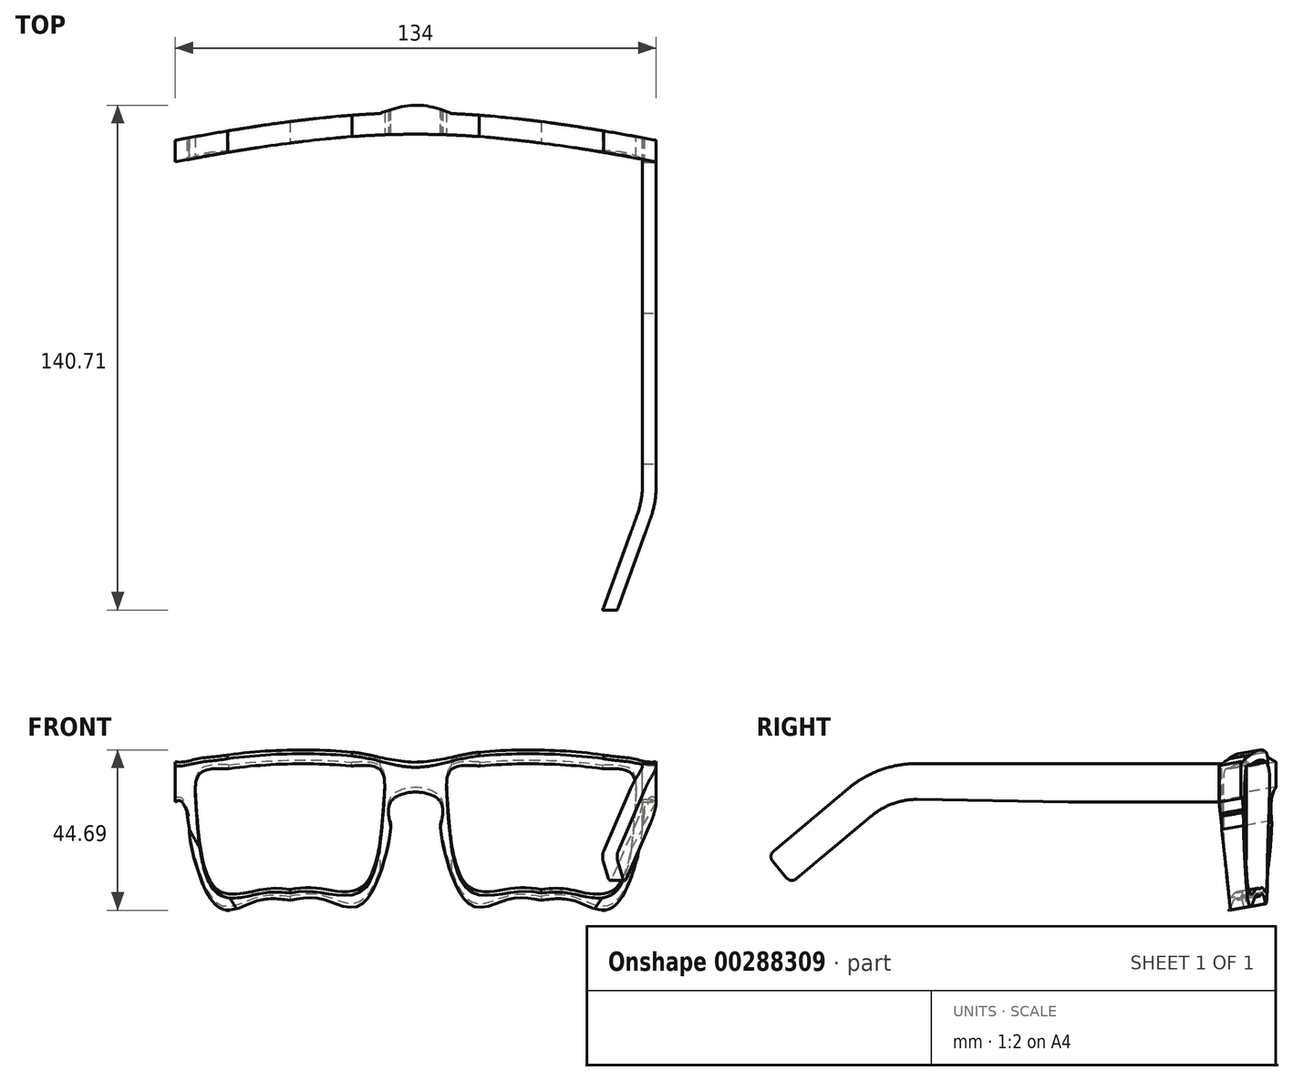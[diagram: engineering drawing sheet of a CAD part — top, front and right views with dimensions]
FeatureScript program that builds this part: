
annotation { "Feature Type Name" : "Feature", "Feature Type Description" : "" }
export const myFeature = defineFeature(function(context is Context, id is Id, definition is map)
    precondition{}
    {
        {
            var Q0;
            Q0=qCreatedBy(makeId("Front.planeOp"),FACE);
            var sketch = newSketch(context, id + "F0", { "sketchPlane" : qUnion([Q0])});
            skLineSegment(sketch, "E0", {"start": v(-67, 0) * mm, "end": v(67, 0) * mm, "construction": true});
            skLineSegment(sketch, "E1", {"start": v(0, -20.5) * mm, "end": v(0, 20.5) * mm, "construction": true});
            skLineSegment(sketch, "E2.bottom", {"start": v(-67, 20.5) * mm, "end": v(67, 20.5) * mm, "construction": true});
            skLineSegment(sketch, "E2.top", {"start": v(-67, -20.5) * mm, "end": v(67, -20.5) * mm, "construction": true});
            skLineSegment(sketch, "E2.left", {"start": v(-67, 20.5) * mm, "end": v(-67, -20.5) * mm, "construction": true});
            skLineSegment(sketch, "E2.right", {"start": v(67, 20.5) * mm, "end": v(67, -20.5) * mm, "construction": true});
            skLineSegment(sketch, "E3", {"start": v(-10, 20.5) * mm, "end": v(10, 20.5) * mm, "construction": true});
            skLineSegment(sketch, "E4", {"start": v(-10, 20.5) * mm, "end": v(-10, -20.5) * mm, "construction": true});
            skLineSegment(sketch, "E5", {"start": v(10, 20.5) * mm, "end": v(10, -20.5) * mm, "construction": true});
            skLineSegment(sketch, "E6", {"start": v(-10, 20.5) * mm, "end": v(-60, 20.5) * mm, "construction": true});
            skLineSegment(sketch, "E7", {"start": v(0, 0) * mm, "end": v(0, 7.8) * mm, "construction": true});
            skLineSegment(sketch, "E8", {"start": v(0, 7.8) * mm, "end": v(0, 15.6) * mm, "construction": true});
            skLineSegment(sketch, "E9", {"start": v(-60, 20.5) * mm, "end": v(-60, -20.5) * mm, "construction": true});
            skLineSegment(sketch, "E10", {"start": v(0, 7.8) * mm, "end": v(-67, 7.8) * mm, "construction": true});
            skLineSegment(sketch, "E11.MirrorCS", {"start": v(0, 15.6) * mm, "end": v(67, 15.6) * mm, "construction": true});
            skLineSegment(sketch, "E12.MirrorCS", {"start": v(0, 7.8) * mm, "end": v(67, 7.8) * mm, "construction": true});
            skPoint(sketch, "E13", {"position": v(-71.63, 0) * mm});
            skPoint(sketch, "E14", {"position": v(-10, 0) * mm});
            skLineSegment(sketch, "E15", {"start": v(-60, 0) * mm, "end": v(-10, 0) * mm, "construction": true});
            skPoint(sketch, "E16", {"position": v(-35, 0) * mm});
            skLineSegment(sketch, "E17", {"start": v(-35, 20.5) * mm, "end": v(-35, -20.5) * mm, "construction": true});
            skLineSegment(sketch, "E18", {"start": v(-35, -20.5) * mm, "end": v(-35, -18.5) * mm, "construction": true});
            skLineSegment(sketch, "E19", {"start": v(-35, -18.5) * mm, "end": v(-35, 17.5) * mm, "construction": true});
            skLineSegment(sketch, "E20", {"start": v(-60, 17.5) * mm, "end": v(-10, 17.5) * mm, "construction": true});
            skLineSegment(sketch, "E21", {"start": v(-35, -18.5) * mm, "end": v(-67, -18.5) * mm, "construction": true});
            skArc(sketch, "E22", {"start": v(-17.95, 16.62) * mm, "mid": v(-35, 17.5) * mm, "end": v(-52.05, 16.62) * mm});
            skFitSpline(sketch, "E23", {"points": [v(-52.05, 16.62) * mm, v(-60, 5.42) * mm, v(-52.82, -14.3) * mm, v(-35, -18.5) * mm], "startDerivative": vector(-80.93, -10.37) * mm, "endDerivative": vector(67.15, -1.23) * mm});
            skFitSpline(sketch, "E24.MirrorCS", {"points": [v(-17.95, 16.62) * mm, v(-10, 5.42) * mm, v(-17.18, -14.3) * mm, v(-35, -18.5) * mm], "startDerivative": vector(80.93, -10.37) * mm, "endDerivative": vector(-67.15, -1.23) * mm});
            skArc(sketch, "E25.MirrorCS", {"start": v(17.95, 16.62) * mm, "mid": v(35, 17.5) * mm, "end": v(52.05, 16.62) * mm});
            skFitSpline(sketch, "E26.MirrorCS", {"points": [v(17.95, 16.62) * mm, v(10, 5.42) * mm, v(17.18, -14.3) * mm, v(35, -18.5) * mm], "startDerivative": vector(-80.93, -10.37) * mm, "endDerivative": vector(67.15, -1.23) * mm});
            skFitSpline(sketch, "E27.MirrorCS", {"points": [v(52.05, 16.62) * mm, v(60, 5.42) * mm, v(52.82, -14.3) * mm, v(35, -18.5) * mm], "startDerivative": vector(80.93, -10.37) * mm, "endDerivative": vector(-67.15, -1.23) * mm});
            skLineSegment(sketch, "E28", {"start": v(-10, 20.5) * mm, "end": v(-7, 20.5) * mm, "construction": true});
            skLineSegment(sketch, "E29", {"start": v(-7, 20.5) * mm, "end": v(-7, -20.5) * mm, "construction": true});
            skLineSegment(sketch, "E30.MirrorCS", {"start": v(7, 20.5) * mm, "end": v(7, -20.5) * mm, "construction": true});
            skFitSpline(sketch, "E31", {"points": [v(-7, 0) * mm, v(0, 7.8) * mm, v(7, 0) * mm], "startDerivative": vector(0, 38.28) * mm, "endDerivative": vector(0, -38.28) * mm});
            skFitSpline(sketch, "E32", {"points": [v(-7, 0) * mm, v(-15.43, -16.34) * mm, v(-35, -20.5) * mm], "startDerivative": vector(0, -10.94) * mm, "endDerivative": vector(-54.71, 0) * mm});
            skFitSpline(sketch, "E33.MirrorCS", {"points": [v(7, 0) * mm, v(15.43, -16.34) * mm, v(35, -20.5) * mm], "startDerivative": vector(0, -10.94) * mm, "endDerivative": vector(54.71, 0) * mm});
            skFitSpline(sketch, "E34.MirrorCS", {"points": [v(-63, 0) * mm, v(-54.57, -16.34) * mm, v(-35, -20.5) * mm], "startDerivative": vector(0, -10.94) * mm, "endDerivative": vector(54.71, 0) * mm});
            skFitSpline(sketch, "E35", {"points": [v(-67, 7.8) * mm, v(-63.86, 5.01) * mm, v(-63, 0) * mm], "startDerivative": vector(11.64, 0) * mm, "endDerivative": vector(3.34, -25.7) * mm});
            skFitSpline(sketch, "E36.MirrorCS", {"points": [v(67, 7.8) * mm, v(63.86, 5.01) * mm, v(63, 0) * mm], "startDerivative": vector(-11.64, 0) * mm, "endDerivative": vector(-3.34, -25.7) * mm});
            skFitSpline(sketch, "E37.MirrorCS", {"points": [v(63, 0) * mm, v(54.57, -16.34) * mm, v(35, -20.5) * mm], "startDerivative": vector(0, -10.94) * mm, "endDerivative": vector(-54.71, 0) * mm});
            skLineSegment(sketch, "E38", {"start": v(-67, 7.8) * mm, "end": v(-67, 20.5) * mm});
            skArc(sketch, "E39.0", {"start": v(-17.67, 19.4) * mm, "mid": v(-35, 20.3) * mm, "end": v(-52.33, 19.4) * mm});
            skArc(sketch, "E40.MirrorCS", {"start": v(17.67, 19.4) * mm, "mid": v(35, 20.3) * mm, "end": v(52.33, 19.4) * mm});
            skFitSpline(sketch, "E41", {"points": [v(-17.67, 19.4) * mm, v(0, 17.22) * mm, v(17.67, 19.4) * mm], "startDerivative": vector(35.33, -6.54) * mm, "endDerivative": vector(35.33, 6.54) * mm});
            skLineSegment(sketch, "E42", {"start": v(67, 7.8) * mm, "end": v(67, 20.5) * mm});
            skFitSpline(sketch, "E43", {"points": [v(67, 17.98) * mm, v(60.54, 18.48) * mm, v(52.33, 19.4) * mm], "startDerivative": vector(-14.43, -1.07) * mm, "endDerivative": vector(-15.93, 1.9) * mm});
            skFitSpline(sketch, "E44.MirrorCS", {"points": [v(-67, 17.98) * mm, v(-60.54, 18.48) * mm, v(-52.33, 19.4) * mm], "startDerivative": vector(14.43, -1.07) * mm, "endDerivative": vector(15.93, 1.9) * mm});
            skSolve(sketch);
        }
        {
            var Q0;
            Q0=qCreatedBy(makeId("Right.planeOp"),FACE);
            var sketch = newSketch(context, id + "F1", { "sketchPlane" : qUnion([Q0])});
            skFitSpline(sketch, "E45.0", {"points": [v(0, 16.62) * mm, v(0, 15.6) * mm, v(0, 5.41) * mm, v(0, -18.1) * mm, v(0, -18.36) * mm, v(0, -18.5) * mm]});
            skPoint(sketch, "E46.0", {"position": v(0, 18.66) * mm});
            skPoint(sketch, "E47.0", {"position": v(0, 20.5) * mm});
            skPoint(sketch, "E48.0", {"position": v(0, -20.5) * mm});
            skLineSegment(sketch, "E49", {"start": v(0, 20.5) * mm, "end": v(46.17, 20.5) * mm, "construction": true});
            skLineSegment(sketch, "E50", {"start": v(0, 20.5) * mm, "end": v(7.4, -21.44) * mm, "construction": true});
            skSolve(sketch);
        }
        {
            var Q0;
            Q0=sQuery(id+"F1.wireOp",EDGE,"E50");
            var Q1;
            Q1=qCreatedBy(makeId("Front.planeOp"),FACE);
            cPlane(context, id + "F2", {"entities" : qUnion([Q0, Q1]), "cplaneType" : CPlaneType.LINE_ANGLE, "offset" : 25.4 * mm, "angle" : 0 * degree, "width" : 152.4 * mm, "height" : 152.4 * mm});
        }
        {
            var Q0;
            Q0=qCreatedBy(id+"F2.planeOp",FACE);
            var sketch = newSketch(context, id + "F3", { "sketchPlane" : qUnion([Q0])});
            skPoint(sketch, "E51.0", {"position": v(-67, 7.68) * mm});
            skPoint(sketch, "E52.0", {"position": v(-63.72, 4.64) * mm});
            skFitSpline(sketch, "E53.0", {"points": [v(-67, 7.68) * mm, v(-65.15, 7.68) * mm, v(-63.28, 3.66) * mm, v(-63.58, 4.42) * mm, v(-63, 0) * mm]});
            skFitSpline(sketch, "E54.0", {"points": [v(-63, 0) * mm, v(-63, -1.76) * mm, v(-55.1, -21.6) * mm, v(-44.31, -20.19) * mm, v(-35, -20.19) * mm]});
            skFitSpline(sketch, "E55.0", {"points": [v(-7, 0) * mm, v(-7, -1.76) * mm, v(-14.9, -21.6) * mm, v(-25.69, -20.19) * mm, v(-35, -20.19) * mm]});
            skFitSpline(sketch, "E56.0", {"points": [v(7, 0) * mm, v(7, 6.28) * mm, v(0, 9.08) * mm, v(-7, 6.28) * mm, v(-7, 0) * mm]});
            skFitSpline(sketch, "E57.0", {"points": [v(7, 0) * mm, v(7, -1.76) * mm, v(14.9, -21.6) * mm, v(25.69, -20.19) * mm, v(35, -20.19) * mm]});
            skFitSpline(sketch, "E58.0", {"points": [v(63, 0) * mm, v(63, -1.76) * mm, v(55.1, -21.6) * mm, v(44.31, -20.19) * mm, v(35, -20.19) * mm]});
            skFitSpline(sketch, "E59.0", {"points": [v(67, 7.68) * mm, v(65.15, 7.68) * mm, v(63.28, 3.66) * mm, v(63.58, 4.42) * mm, v(63, 0) * mm]});
            skEllipticalArc(sketch, "E60.0", {});
            skFitSpline(sketch, "E61.0", {"points": [v(17.67, 19.1) * mm, v(11.78, 18.03) * mm, v(0, 15.88) * mm, v(-11.78, 18.03) * mm, v(-17.67, 19.1) * mm]});
            skEllipticalArc(sketch, "E62.0", {});
            skFitSpline(sketch, "E63.0", {"points": [v(-52.05, 16.37) * mm, v(-60, 15.36) * mm, v(-61.12, 5.33) * mm, v(-55.22, -17.83) * mm, v(-42.62, -18.08) * mm, v(-35, -18.22) * mm]});
            skFitSpline(sketch, "E64.0", {"points": [v(-17.95, 16.37) * mm, v(-10, 15.36) * mm, v(-8.88, 5.33) * mm, v(-14.78, -17.83) * mm, v(-27.38, -18.08) * mm, v(-35, -18.22) * mm]});
            skFitSpline(sketch, "E65.0", {"points": [v(-17.95, 16.37) * mm, v(-10, 15.36) * mm, v(-8.88, 5.33) * mm, v(-14.78, -17.83) * mm, v(-27.38, -18.08) * mm, v(-35, -18.22) * mm]});
            skFitSpline(sketch, "E66.0", {"points": [v(17.95, 16.37) * mm, v(10, 15.36) * mm, v(8.88, 5.33) * mm, v(14.78, -17.83) * mm, v(27.38, -18.08) * mm, v(35, -18.22) * mm]});
            skFitSpline(sketch, "E67.0", {"points": [v(52.05, 16.37) * mm, v(60, 15.36) * mm, v(61.12, 5.33) * mm, v(55.22, -17.83) * mm, v(42.62, -18.08) * mm, v(35, -18.22) * mm]});
            skFitSpline(sketch, "E68.0", {"points": [v(-67, 17.7) * mm, v(-64.74, 17.54) * mm, v(-60.55, 18.32) * mm, v(-55.15, 18.77) * mm, v(-52.33, 19.1) * mm]});
            skFitSpline(sketch, "E69.0", {"points": [v(67, 17.7) * mm, v(64.74, 17.54) * mm, v(60.55, 18.32) * mm, v(55.15, 18.77) * mm, v(52.33, 19.1) * mm]});
            skEllipticalArc(sketch, "E70.0.0", {});
            skFitSpline(sketch, "E70.0.1", {"points": [v(-17.67, 19.1) * mm, v(-11.78, 18.03) * mm, v(0, 15.88) * mm, v(11.78, 18.03) * mm, v(17.67, 19.1) * mm]});
            skFitSpline(sketch, "E70.0.3", {"points": [v(52.33, 19.1) * mm, v(55.15, 18.77) * mm, v(60.55, 18.32) * mm, v(64.74, 17.54) * mm, v(67, 17.7) * mm]});
            skLineSegment(sketch, "E70.0.4", {"start": v(67, 17.7) * mm, "end": v(67, 7.68) * mm});
            skFitSpline(sketch, "E70.0.5", {"points": [v(67, 7.68) * mm, v(65.15, 7.68) * mm, v(63.28, 3.66) * mm, v(63.58, 4.42) * mm, v(63, 0) * mm]});
            skFitSpline(sketch, "E70.0.6", {"points": [v(63, 0) * mm, v(63, -1.76) * mm, v(55.1, -21.6) * mm, v(44.31, -20.19) * mm, v(35, -20.19) * mm]});
            skFitSpline(sketch, "E70.0.7", {"points": [v(35, -20.19) * mm, v(25.69, -20.19) * mm, v(14.9, -21.6) * mm, v(7, -1.76) * mm, v(7, 0) * mm]});
            skFitSpline(sketch, "E70.0.8", {"points": [v(7, 0) * mm, v(7, 6.28) * mm, v(0, 9.08) * mm, v(-7, 6.28) * mm, v(-7, 0) * mm]});
            skFitSpline(sketch, "E70.0.9", {"points": [v(-7, 0) * mm, v(-7, -1.76) * mm, v(-14.9, -21.6) * mm, v(-25.69, -20.19) * mm, v(-35, -20.19) * mm]});
            skFitSpline(sketch, "E70.0.10", {"points": [v(-35, -20.19) * mm, v(-44.31, -20.19) * mm, v(-55.1, -21.6) * mm, v(-63, -1.76) * mm, v(-63, 0) * mm]});
            skFitSpline(sketch, "E70.0.11", {"points": [v(-63, 0) * mm, v(-63.58, 4.42) * mm, v(-63.28, 3.66) * mm, v(-65.15, 7.68) * mm, v(-67, 7.68) * mm]});
            skLineSegment(sketch, "E70.0.12", {"start": v(-67, 7.68) * mm, "end": v(-67, 17.7) * mm});
            skFitSpline(sketch, "E70.0.13", {"points": [v(-67, 17.7) * mm, v(-64.74, 17.54) * mm, v(-60.55, 18.32) * mm, v(-55.15, 18.77) * mm, v(-52.33, 19.1) * mm]});
            const initialGuessF3  = {"E60.0": [0.035, -0.14567639106445007, 1, 0, 0.1682176836736388, 0.1656620790755546, 1.467573942796451, 1.6740187107933424], "E62.0": [-0.035, -0.14567639106445007, -1, 0, 0.1682176836736388, 0.1656620790755546, 4.609166596386244, 4.815611364383136], "E62.0": [-0.035, -0.14567639106445007, -1, 0, 0.16542368421031978, 0.1629105267421661, 4.6091665963862285, 4.81561136438315], "E60.0": [0.035, -0.14567639106445007, 1, 0, 0.16542368421031978, 0.1629105267421661, 1.4675739427964356, 1.6740187107933577], "E70.0.0": [-0.035, -0.14567639106445007, 1, 0, 0.1682176836736388, 0.1656620790755546, 1.467573942796343, 1.6740187107934503], "E60.0": [0.035, -0.14567639106445007, 1, 0, 0.1682176836736388, 0.1656620790755546, 1.467573942796343, 1.6740187107934503]};
            skSetInitialGuess(sketch, initialGuessF3);
            skSolve(sketch);
        }
        {
            var Q0;
            Q0 = qSketchRegion(id + "F3", true);
            extrude(context, id + "F4", {"entities" : qUnion([Q0]), "depth" : 19.8 * mm, "hasSecondDirection" : true, "secondDirectionOppositeDirection" : true, "secondDirectionDepth" : 15.5 * mm});
        }
        {
            var Q0;
            Q0=qCreatedBy(makeId("Top.planeOp"),FACE);
            var sketch = newSketch(context, id + "F5", { "sketchPlane" : qUnion([Q0])});
            skPoint(sketch, "E71.0.internal.snap0", {"position": v(-82.32, 2.82) * mm});
            skPoint(sketch, "E71.2.internal.snap0", {"position": v(82.43, 2.82) * mm});
            skFitSpline(sketch, "E71", {"points": [v(-82.32, 0) * mm, v(0, 10.6) * mm, v(82.43, 0) * mm], "startDerivative": vector(164.67, 31.78) * mm, "endDerivative": vector(164.84, -31.78) * mm});
            skFitSpline(sketch, "E72.0", {"points": [v(-81.18, -5.9) * mm, v(-74.32, -4.57) * mm, v(-60.65, -1.93) * mm, v(-43.67, 0.94) * mm, v(-30.15, 2.73) * mm, v(-20.05, 3.77) * mm, v(-11.67, 4.32) * mm, v(-4.98, 4.55) * mm, v(0.03, 4.61) * mm, v(5.03, 4.55) * mm, v(11.73, 4.32) * mm, v(20.11, 3.76) * mm, v(30.22, 2.73) * mm, v(43.74, 0.94) * mm, v(60.74, -1.93) * mm, v(74.43, -4.57) * mm, v(81.3, -5.9) * mm]});
            skFitSpline(sketch, "E73", {"points": [v(-10, 10.37) * mm, v(0, 12.7) * mm, v(10, 10.37) * mm], "startDerivative": vector(30, 11.53) * mm, "endDerivative": vector(30, -12.13) * mm});
            skFitSpline(sketch, "E74", {"points": [v(-5, 4.53) * mm, v(0, 5.51) * mm, v(5, 4.53) * mm], "startDerivative": vector(10, 2.93) * mm, "endDerivative": vector(10, -2.93) * mm});
            skFitSpline(sketch, "E75.trimOffspring", {"points": [v(-81.18, -5.9) * mm, v(-74.32, -4.57) * mm, v(-60.65, -1.93) * mm, v(-43.67, 0.94) * mm, v(-30.15, 2.73) * mm, v(-20.05, 3.77) * mm, v(-11.67, 4.32) * mm, v(-4.98, 4.55) * mm, v(0.03, 4.61) * mm, v(5.03, 4.55) * mm, v(11.73, 4.32) * mm, v(20.11, 3.76) * mm, v(30.22, 2.73) * mm, v(43.74, 0.94) * mm, v(60.74, -1.93) * mm, v(74.43, -4.57) * mm, v(81.3, -5.9) * mm]});
            skLineSegment(sketch, "E76", {"start": v(-82.32, 0) * mm, "end": v(-81.18, -5.9) * mm});
            skLineSegment(sketch, "E77", {"start": v(81.3, -5.9) * mm, "end": v(82.43, 0) * mm});
            skSolve(sketch);
        }
        {
            var Q0;
            Q0 = qSketchRegion(id + "F5", true);
            extrude(context, id + "F6", {"entities" : qUnion([Q0]), "operationType" : NewBodyOperationType.INTERSECT, "depth" : 47.75 * mm, "hasSecondDirection" : true, "secondDirectionOppositeDirection" : true, "secondDirectionDepth" : 62.74 * mm});
        }
        {
            var Q0;
            Q0=qCreatedBy(makeId("Top.planeOp"),FACE);
            var Q1;
            Q1=sQuery(id+"F0.wireOp",VERTEX,"E44.MirrorCS.0.internal");
            cPlane(context, id + "F7", {"entities" : qUnion([Q0, Q1]), "cplaneType" : CPlaneType.PLANE_POINT, "offset" : 25.4 * mm, "width" : 152.4 * mm, "height" : 152.4 * mm});
        }
        {
            var Q0;
            Q0=qCreatedBy(id+"F7.planeOp",FACE);
            var sketch = newSketch(context, id + "F8", { "sketchPlane" : qUnion([Q0])});
            skLineSegment(sketch, "E78.0.0", {"start": v(-52.33, -0.55) * mm, "end": v(-52.33, 5.53) * mm});
            skLineSegment(sketch, "E79.0.1", {"start": v(-52.33, 5.53) * mm, "end": v(-52.33, -0.55) * mm});
            skLineSegment(sketch, "E79.0.3", {"start": v(-17.67, 3.9) * mm, "end": v(-17.67, 9.91) * mm});
            skLineSegment(sketch, "E80.0.0", {"start": v(17.67, 3.9) * mm, "end": v(17.67, 9.92) * mm});
            skLineSegment(sketch, "E80.0.4", {"start": v(-17.67, 9.91) * mm, "end": v(-17.67, 3.9) * mm});
            skLineSegment(sketch, "E81.0.0", {"start": v(17.67, 9.92) * mm, "end": v(17.67, 3.9) * mm});
            skLineSegment(sketch, "E81.0.2", {"start": v(52.33, -0.54) * mm, "end": v(52.33, 5.54) * mm});
            skLineSegment(sketch, "E82.0.3", {"start": v(52.33, 5.54) * mm, "end": v(52.33, -0.54) * mm});
            skLineSegment(sketch, "E83", {"start": v(-67, -3.18) * mm, "end": v(-67, -98.18) * mm});
            skLineSegment(sketch, "E84", {"start": v(-67, -138.18) * mm, "end": v(-63.2, -138.18) * mm});
            skLineSegment(sketch, "E85", {"start": v(-63.2, -93) * mm, "end": v(-63.2, -2.48) * mm});
            skLineSegment(sketch, "E86", {"start": v(-65.47, -102.39) * mm, "end": v(-52.44, -138.18) * mm});
            skLineSegment(sketch, "E87.0", {"start": v(-61.67, -101.7) * mm, "end": v(-48.86, -136.88) * mm});
            skLineSegment(sketch, "E88", {"start": v(-52.44, -138.18) * mm, "end": v(-48.86, -136.88) * mm});
            skPoint(sketch, "E89.visualSharp", {"position": v(-63.2, -97.48) * mm});
            skArc(sketch, "E89.filletArc", {"start": v(-63.2, -93) * mm, "mid": v(-62.81, -97.41) * mm, "end": v(-61.67, -101.7) * mm});
            skPoint(sketch, "E90.visualSharp", {"position": v(-67, -98.18) * mm});
            skArc(sketch, "E90.filletArc", {"start": v(-67, -93.7) * mm, "mid": v(-66.61, -98.11) * mm, "end": v(-65.47, -102.39) * mm});
            skFitSpline(sketch, "E91.0", {"points": [v(-52.33, -0.55) * mm, v(-53.55, -0.76) * mm, v(-56, -1.18) * mm, v(-59.67, -1.83) * mm, v(-63.3, -2.5) * mm, v(-65.76, -2.95) * mm, v(-67, -3.18) * mm]});
            skLineSegment(sketch, "E92.MirrorCS", {"start": v(67, -3.18) * mm, "end": v(67, -98.18) * mm});
            skLineSegment(sketch, "E93.MirrorCS", {"start": v(63.2, -93) * mm, "end": v(63.2, -2.48) * mm});
            skArc(sketch, "E94.MirrorCS", {"start": v(67, -93.7) * mm, "mid": v(66.61, -98.11) * mm, "end": v(65.47, -102.39) * mm});
            skArc(sketch, "E95.MirrorCS", {"start": v(63.2, -93) * mm, "mid": v(62.81, -97.41) * mm, "end": v(61.67, -101.7) * mm});
            skLineSegment(sketch, "E96.MirrorCS", {"start": v(65.47, -102.39) * mm, "end": v(52.44, -138.18) * mm});
            skLineSegment(sketch, "E97.MirrorCS", {"start": v(61.67, -101.7) * mm, "end": v(48.86, -136.88) * mm});
            skLineSegment(sketch, "E98.MirrorCS", {"start": v(52.44, -138.18) * mm, "end": v(48.86, -136.88) * mm});
            skLineSegment(sketch, "E99", {"start": v(63.2, -2.48) * mm, "end": v(67, -3.18) * mm});
            skSolve(sketch);
        }
        {
            var Q0;
            {var subQ4=sQuery(id+"F8.wireOp",EDGE,"E85");Q0=makeQuery(id+"F8.imprint","IMPRINT",FACE,{"disambiguationData":[TD([[makeQuery(id+"F8.imprint","IMPRINT",EDGE,{"derivedFrom":subQ4}),1.0]])]});}
            var Q1;
            Q1=makeQuery(id+"F8.imprint","IMPRINT",FACE,{"disambiguationData":[TD([[makeQuery(id+"F8.imprint","IMPRINT",EDGE,{"derivedFrom":sQuery(id+"F8.wireOp",EDGE,"E93.MirrorCS")}),-1.0]])]});
            extrude(context, id + "F9", {"entities" : qUnion([Q0, Q1]), "oppositeDirection" : true, "depth" : 36.58 * mm});
        }
        {
            var Q0;
            Q0=qCreatedBy(makeId("Right.planeOp"),FACE);
            var sketch = newSketch(context, id + "F10", { "sketchPlane" : qUnion([Q0])});
            skLineSegment(sketch, "E100.0.6", {"start": v(-87.26, 17.98) * mm, "end": v(-3.18, 17.98) * mm});
            skLineSegment(sketch, "E101.0.0", {"start": v(-146.92, 17.98) * mm, "end": v(-138.18, 17.98) * mm});
            skLineSegment(sketch, "E101.0.3", {"start": v(-138.18, -18.6) * mm, "end": v(-138.18, 17.98) * mm});
            skLineSegment(sketch, "E102", {"start": v(-3.18, 17.98) * mm, "end": v(-87.26, 17.98) * mm});
            skLineSegment(sketch, "E103", {"start": v(-106.55, 10.96) * mm, "end": v(-127.32, -6.47) * mm, "construction": true});
            skPoint(sketch, "E104.visualSharp", {"position": v(-98.18, 17.98) * mm});
            skArc(sketch, "E104.filletArc", {"start": v(-87.26, 17.98) * mm, "mid": v(-97.52, 16.17) * mm, "end": v(-106.55, 10.96) * mm});
            skLineSegment(sketch, "E105", {"start": v(-106.55, 10.96) * mm, "end": v(-128.82, -7.73) * mm});
            skArc(sketch, "E106.0", {"start": v(-87.26, 7.98) * mm, "mid": v(-94.1, 6.77) * mm, "end": v(-100.12, 3.3) * mm});
            skLineSegment(sketch, "E107", {"start": v(-3.18, 7.24) * mm, "end": v(-45.22, 7.24) * mm, "construction": true});
            skPoint(sketch, "E107.endSnap0", {"position": v(-45.22, 5.98) * mm});
            skLineSegment(sketch, "E108", {"start": v(-45.22, 7.24) * mm, "end": v(-87.26, 7.98) * mm, "construction": true});
            skLineSegment(sketch, "E109.0", {"start": v(-100.12, 3.3) * mm, "end": v(-120.9, -14.13) * mm, "construction": true});
            skLineSegment(sketch, "E110", {"start": v(-3.18, 7.24) * mm, "end": v(-45.22, 7.24) * mm});
            skLineSegment(sketch, "E111", {"start": v(-87.26, 7.98) * mm, "end": v(-45.22, 7.24) * mm});
            skLineSegment(sketch, "E112", {"start": v(-122.4, -15.4) * mm, "end": v(-100.12, 3.3) * mm});
            skLineSegment(sketch, "E113", {"start": v(-123.65, -13.9) * mm, "end": v(-127.56, -9.23) * mm});
            skPoint(sketch, "E114.visualSharp", {"position": v(-122.4, -15.4) * mm});
            skArc(sketch, "E114.filletArc", {"start": v(-123.65, -13.9) * mm, "mid": v(-122.32, -14.59) * mm, "end": v(-120.9, -14.13) * mm});
            skPoint(sketch, "E115.visualSharp", {"position": v(-128.82, -7.73) * mm});
            skArc(sketch, "E115.filletArc", {"start": v(-127.32, -6.47) * mm, "mid": v(-128.01, -7.8) * mm, "end": v(-127.56, -9.23) * mm});
            skLineSegment(sketch, "E116", {"start": v(0, -22.9) * mm, "end": v(-146.92, -22.9) * mm});
            skLineSegment(sketch, "E117", {"start": v(-146.92, -22.9) * mm, "end": v(-146.92, 23.55) * mm});
            skLineSegment(sketch, "E118", {"start": v(-146.92, 23.55) * mm, "end": v(-3.18, 23.55) * mm});
            skLineSegment(sketch, "E119", {"start": v(-3.18, 23.55) * mm, "end": v(-3.18, 17.98) * mm});
            skPoint(sketch, "E120.orphan", {"position": v(-93.7, 17.98) * mm});
            skPoint(sketch, "E121.orphan", {"position": v(-102.39, 17.98) * mm});
            skPoint(sketch, "E100.0.0.end.orphan", {"position": v(2.92, 18.5) * mm});
            skPoint(sketch, "E100.0.2.start.orphan", {"position": v(2.92, 8.32) * mm});
            skPoint(sketch, "E100.0.7.end.orphan", {"position": v(-3.18, 17.42) * mm});
            skLineSegment(sketch, "E122", {"start": v(0, -22.9) * mm, "end": v(-3.18, 7.24) * mm});
            skLineSegment(sketch, "E123", {"start": v(-3.18, 7.24) * mm, "end": v(-3.18, 7.24) * mm});
            skSolve(sketch);
        }
        {
            var Q0;
            Q0 = qSketchRegion(id + "F10", true);
            extrude(context, id + "F11", {"entities" : qUnion([Q0]), "operationType" : NewBodyOperationType.REMOVE, "oppositeDirection" : true, "depth" : 90.93 * mm, "hasSecondDirection" : true, "secondDirectionOppositeDirection" : false, "secondDirectionDepth" : 124.46 * mm});
        }
    });
